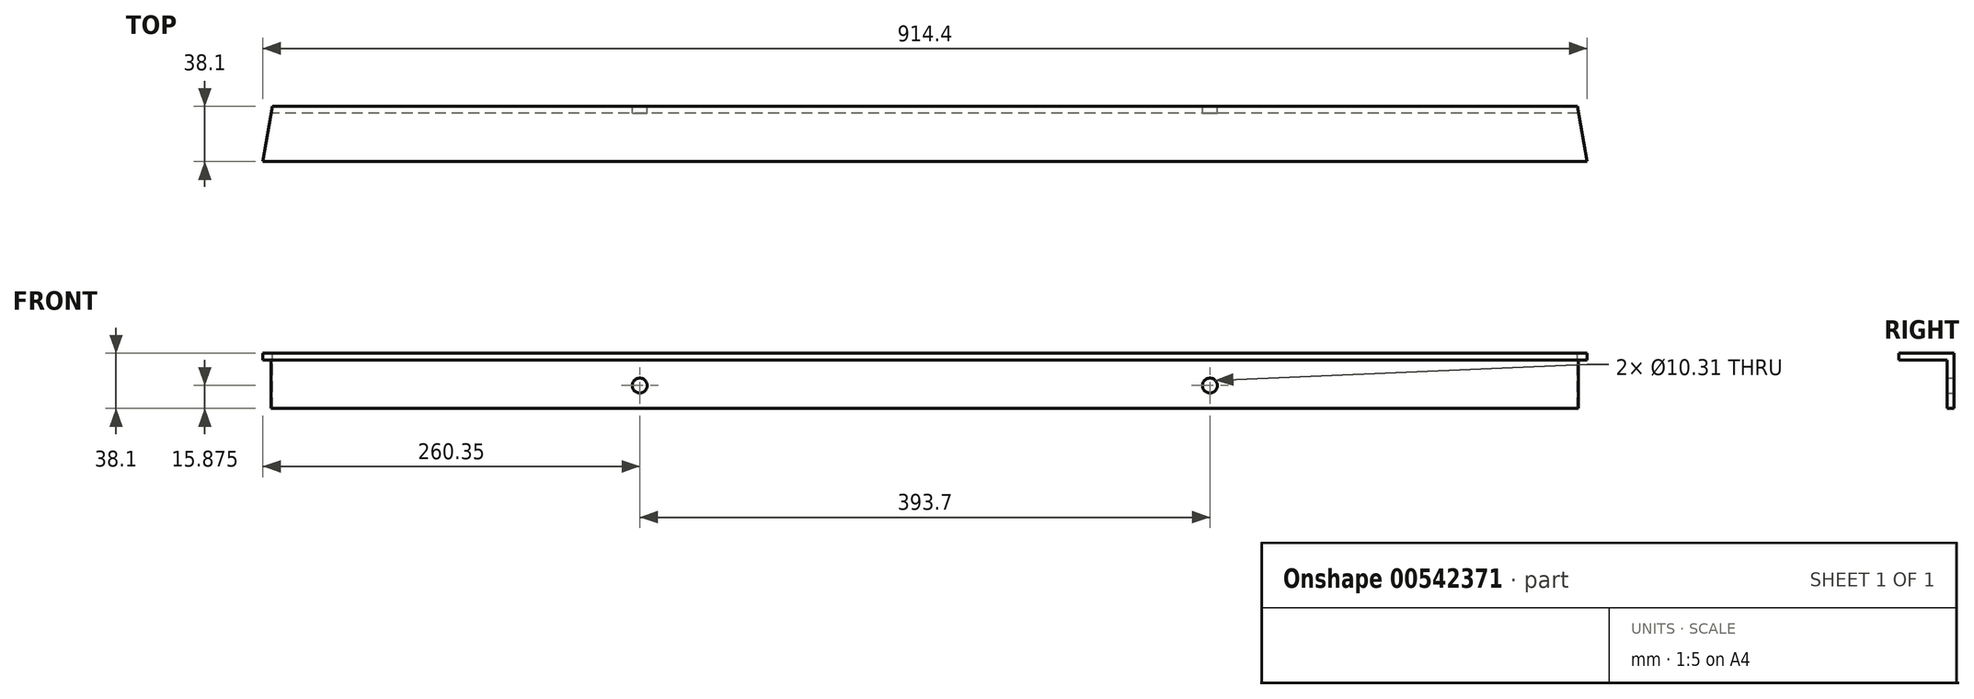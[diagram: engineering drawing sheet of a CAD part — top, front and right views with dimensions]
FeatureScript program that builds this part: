
annotation { "Feature Type Name" : "Feature", "Feature Type Description" : "" }
export const myFeature = defineFeature(function(context is Context, id is Id, definition is map)
    precondition{}
    {
        {
            var Q0;
            Q0=qCreatedBy(makeId("Front.planeOp"),FACE);
            var sketch = newSketch(context, id + "F0", { "sketchPlane" : qUnion([Q0])});
            skLineSegment(sketch, "E0.bottom", {"start": v(457.2, -19.05) * mm, "end": v(-457.2, -19.05) * mm});
            skLineSegment(sketch, "E0.top", {"start": v(457.2, 19.05) * mm, "end": v(-457.2, 19.05) * mm});
            skLineSegment(sketch, "E0.left", {"start": v(457.2, -19.05) * mm, "end": v(457.2, 19.05) * mm});
            skLineSegment(sketch, "E0.right", {"start": v(-457.2, -19.05) * mm, "end": v(-457.2, 19.05) * mm});
            skPoint(sketch, "E0.middle", {"position": v(0, 0) * mm});
            skCircle(sketch, "E1", {"center": v(-196.85, -3.18) * mm, "radius": 5.16 * mm});
            skCircle(sketch, "E2", {"center": v(196.85, -3.17) * mm, "radius": 5.16 * mm});
            skSolve(sketch);
        }
        {
            var Q0;
            Q0=makeQuery(id+"F0.imprint","IMPRINT",FACE,{"disambiguationData":[TD([[makeQuery(id+"F0.imprint","IMPRINT",EDGE,{"derivedFrom":sQuery(id+"F0.wireOp",EDGE,"E0.bottom")}),-1.0]])]});
            extrude(context, id + "F1", {"entities" : qUnion([Q0]), "depth" : 4.76 * mm, "offsetDistance" : 25.4 * mm});
        }
        {
            var Q0;
            Q0=makeQuery(id+"F1.opExtrude","CAP_FACE",FACE,{"disambiguationData":[OSD([sQuery(id+"F0.wireOp",EDGE,"E0.bottom"),sQuery(id+"F0.wireOp",EDGE,"E0.top"),sQuery(id+"F0.wireOp",EDGE,"E0.left"),sQuery(id+"F0.wireOp",EDGE,"E0.right"),sQuery(id+"F0.wireOp",EDGE,"E1"),sQuery(id+"F0.wireOp",EDGE,"E2")])],"isStart":false});
            var sketch = newSketch(context, id + "F2", { "sketchPlane" : qUnion([Q0])});
            skLineSegment(sketch, "E3.bottom", {"start": v(-457.2, 19.05) * mm, "end": v(457.2, 19.05) * mm});
            skLineSegment(sketch, "E3.top", {"start": v(-457.2, 14.29) * mm, "end": v(457.2, 14.29) * mm});
            skLineSegment(sketch, "E3.left", {"start": v(-457.2, 19.05) * mm, "end": v(-457.2, 14.29) * mm});
            skLineSegment(sketch, "E3.right", {"start": v(457.2, 19.05) * mm, "end": v(457.2, 14.29) * mm});
            skSolve(sketch);
        }
        {
            var Q0;
            Q0=makeQuery(id+"F2.imprint","IMPRINT",FACE,{"disambiguationData":[TD([[makeQuery(id+"F2.imprint","IMPRINT",EDGE,{"derivedFrom":sQuery(id+"F2.wireOp",EDGE,"E3.bottom")}),1.0]])]});
            extrude(context, id + "F3", {"entities" : qUnion([Q0]), "operationType" : NewBodyOperationType.ADD, "depth" : 33.34 * mm, "offsetDistance" : 25.4 * mm});
        }
        {
            var Q0;
            Q0=makeQuery(id+"F3.boolean.opBoolean","MERGE",FACE,{"derivedFrom":[makeQuery(id+"F1.opExtrude","SWEPT_FACE",FACE,{"disambiguationData":[OSD([sQuery(id+"F0.wireOp",EDGE,"E0.top")])]}),makeQuery(id+"F3.opExtrude","SWEPT_FACE",FACE,{"disambiguationData":[OSD([sQuery(id+"F2.wireOp",EDGE,"E3.bottom")])]})]});
            var sketch = newSketch(context, id + "F4", { "sketchPlane" : qUnion([Q0])});
            skLineSegment(sketch, "E4", {"start": v(457.2, -38.1) * mm, "end": v(450.48, 0) * mm});
            skLineSegment(sketch, "E5", {"start": v(-457.2, -38.1) * mm, "end": v(-450.48, 0) * mm});
            skSolve(sketch);
        }
        {
            var Q0;
            {var subQ0=sQuery(id+"F4.wireOp",EDGE,"E4");Q0=makeQuery(id+"F4.imprint","IMPRINT",FACE,{"disambiguationData":[TD([[makeQuery(id+"F4.imprint","IMPRINT",EDGE,{"derivedFrom":subQ0}),-1.0]])]});}
            var Q1;
            {var subQ0=sQuery(id+"F4.wireOp",EDGE,"E5");Q1=makeQuery(id+"F4.imprint","IMPRINT",FACE,{"disambiguationData":[TD([[makeQuery(id+"F4.imprint","IMPRINT",EDGE,{"derivedFrom":subQ0}),1.0]])]});}
            extrude(context, id + "F5", {"entities" : qUnion([Q0, Q1]), "operationType" : NewBodyOperationType.REMOVE, "oppositeDirection" : true, "depth" : 38.1 * mm, "offsetDistance" : 25.4 * mm});
        }
    });
